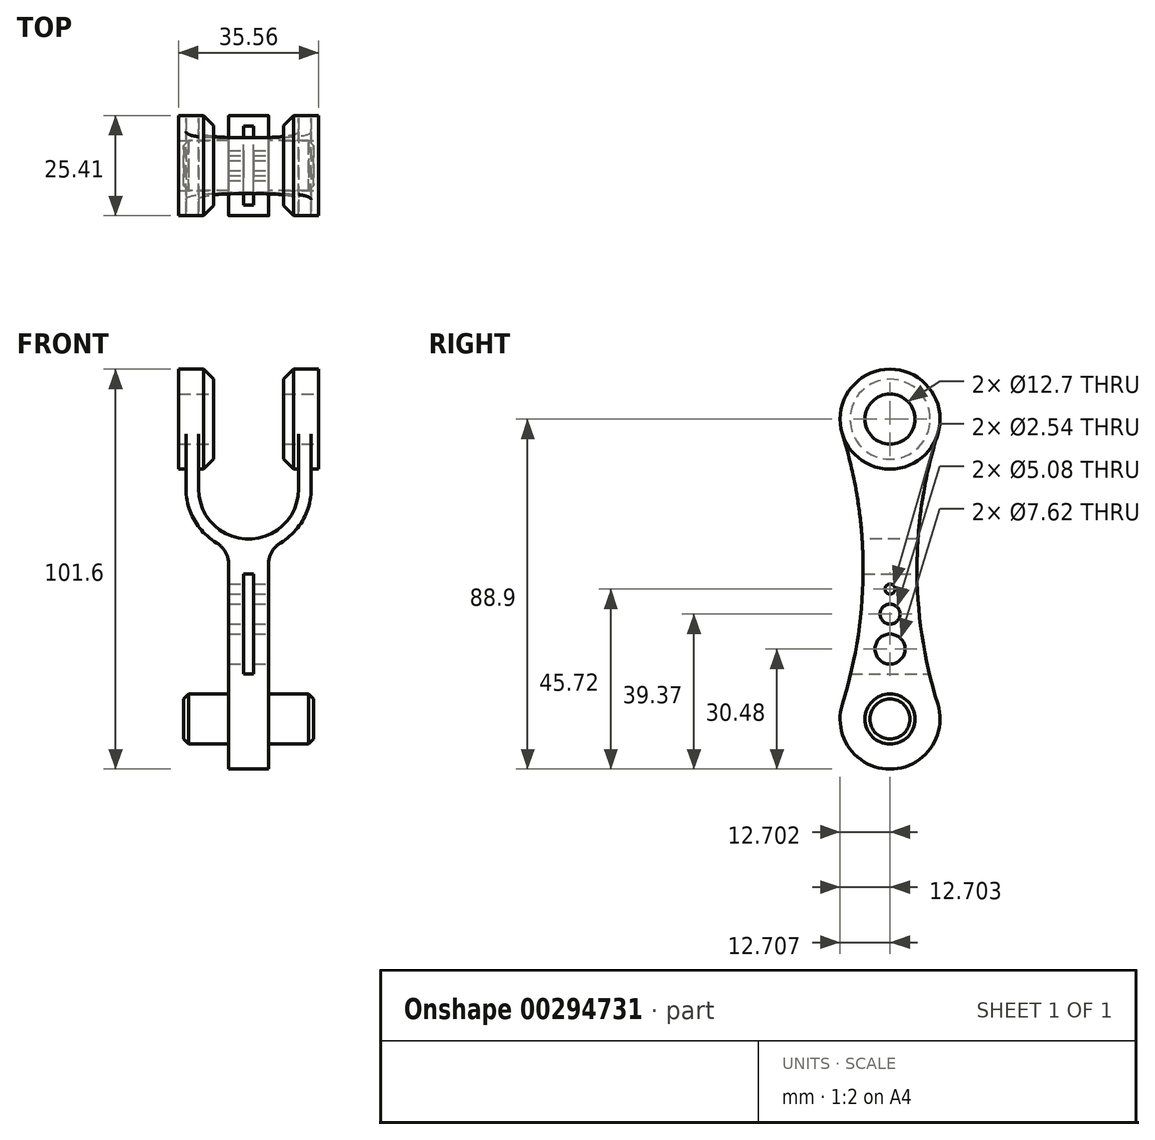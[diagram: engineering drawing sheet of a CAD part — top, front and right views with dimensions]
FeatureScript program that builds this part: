
annotation { "Feature Type Name" : "Feature", "Feature Type Description" : "" }
export const myFeature = defineFeature(function(context is Context, id is Id, definition is map)
    precondition{}
    {
        {
            var Q0;
            Q0=qCreatedBy(makeId("Front.planeOp"),FACE);
            var sketch = newSketch(context, id + "F0", { "sketchPlane" : qUnion([Q0])});
            skPoint(sketch, "E0.middle", {"position": v(0, 0) * mm});
            skArc(sketch, "E1", {"start": v(-8.17, -19.4) * mm, "mid": v(-13.82, -25.2) * mm, "end": v(-15.88, -33.02) * mm});
            skLineSegment(sketch, "E2.bottom", {"start": v(-5.08, 2.35) * mm, "end": v(5.08, 2.35) * mm});
            skLineSegment(sketch, "E2.left", {"start": v(-5.08, 2.35) * mm, "end": v(-5.08, -13.95) * mm});
            skLineSegment(sketch, "E2.right", {"start": v(5.08, 2.35) * mm, "end": v(5.08, -13.95) * mm});
            skArc(sketch, "E3", {"start": v(12.7, -33.02) * mm, "mid": v(0, -20.32) * mm, "end": v(-12.7, -33.02) * mm});
            skLineSegment(sketch, "E4.top", {"start": v(14.22, -50.8) * mm, "end": v(14.36, -50.8) * mm});
            skLineSegment(sketch, "E4.left", {"start": v(12.7, -33.02) * mm, "end": v(12.7, -49.28) * mm});
            skLineSegment(sketch, "E4.right", {"start": v(15.88, -33.02) * mm, "end": v(15.88, -49.28) * mm});
            skLineSegment(sketch, "E5.top", {"start": v(-14.36, -50.8) * mm, "end": v(-14.22, -50.8) * mm});
            skLineSegment(sketch, "E5.left", {"start": v(-15.88, -33.02) * mm, "end": v(-15.88, -49.28) * mm});
            skLineSegment(sketch, "E5.right", {"start": v(-12.7, -33.02) * mm, "end": v(-12.7, -49.28) * mm});
            skArc(sketch, "E6.trimOffspring", {"start": v(15.88, -33.02) * mm, "mid": v(13.82, -25.2) * mm, "end": v(8.17, -19.4) * mm});
            skPoint(sketch, "E7.visualSharp", {"position": v(-5.08, -17.97) * mm});
            skArc(sketch, "E7.filletArc", {"start": v(-8.17, -19.4) * mm, "mid": v(-5.9, -17.08) * mm, "end": v(-5.08, -13.95) * mm});
            skPoint(sketch, "E8.visualSharp", {"position": v(5.08, -17.97) * mm});
            skArc(sketch, "E8.filletArc", {"start": v(5.08, -13.95) * mm, "mid": v(5.9, -17.08) * mm, "end": v(8.17, -19.4) * mm});
            skArc(sketch, "E9.filletArc", {"start": v(12.7, -49.28) * mm, "mid": v(13.15, -50.35) * mm, "end": v(14.22, -50.8) * mm});
            skArc(sketch, "E10.filletArc", {"start": v(14.36, -50.8) * mm, "mid": v(15.44, -50.35) * mm, "end": v(15.88, -49.28) * mm});
            skArc(sketch, "E11.filletArc", {"start": v(-15.88, -49.28) * mm, "mid": v(-15.44, -50.35) * mm, "end": v(-14.36, -50.8) * mm});
            skArc(sketch, "E12.filletArc", {"start": v(-14.22, -50.8) * mm, "mid": v(-13.15, -50.35) * mm, "end": v(-12.7, -49.28) * mm});
            skSolve(sketch);
        }
        {
            var Q0;
            Q0=qSketchRegion(id+"F0",true);
            extrude(context, id + "F1", {"entities" : qUnion([Q0]), "endBound" : BoundingType.SYMMETRIC, "depth" : 38.1 * mm});
        }
        {
            var Q0;
            Q0=qCreatedBy(makeId("Right.planeOp"),FACE);
            var sketch = newSketch(context, id + "F2", { "sketchPlane" : qUnion([Q0])});
            skCircle(sketch, "E13", {"center": v(0, -50.8) * mm, "radius": 6.35 * mm});
            skSolve(sketch);
        }
        {
            var Q0;
            Q0=qCreatedBy(makeId("Right.planeOp"),FACE);
            var sketch = newSketch(context, id + "F3", { "sketchPlane" : qUnion([Q0])});
            skCircle(sketch, "E14", {"center": v(0, -50.8) * mm, "radius": 12.7 * mm});
            skSolve(sketch);
        }
        {
            var Q0;
            Q0=qSketchRegion(id+"F3",true);
            extrude(context, id + "F4", {"entities" : qUnion([Q0]), "operationType" : NewBodyOperationType.ADD, "endBound" : BoundingType.SYMMETRIC, "depth" : 35.56 * mm});
        }
        {
            var Q0;
            Q0=qCreatedBy(makeId("Front.planeOp"),FACE);
            var sketch = newSketch(context, id + "F5", { "sketchPlane" : qUnion([Q0])});
            skLineSegment(sketch, "E15.bottom", {"start": v(8.9, -69.85) * mm, "end": v(-8.89, -69.85) * mm});
            skLineSegment(sketch, "E15.top", {"start": v(8.9, -31.75) * mm, "end": v(-8.89, -31.75) * mm});
            skLineSegment(sketch, "E15.left", {"start": v(8.9, -69.85) * mm, "end": v(8.9, -31.75) * mm});
            skLineSegment(sketch, "E15.right", {"start": v(-8.89, -69.85) * mm, "end": v(-8.89, -31.75) * mm});
            skPoint(sketch, "E15.middle", {"position": v(0, -50.8) * mm});
            skSolve(sketch);
        }
        {
            var Q0;
            Q0=qSketchRegion(id+"F2",true);
            extrude(context, id + "F6", {"entities" : qUnion([Q0]), "operationType" : NewBodyOperationType.REMOVE, "endBound" : BoundingType.SYMMETRIC, "oppositeDirection" : true, "depth" : 76.2 * mm});
        }
        {
            var Q0;
            Q0=qSketchRegion(id+"F5",true);
            extrude(context, id + "F7", {"entities" : qUnion([Q0]), "operationType" : NewBodyOperationType.REMOVE, "endBound" : BoundingType.SYMMETRIC, "oppositeDirection" : true, "depth" : 38.1 * mm});
        }
        {
            var Q0;
            Q0=makeQuery(id+"F7.boolean.opBoolean","INTERSECT",EDGE,{"derivedFrom":[makeQuery(id+"F4.opExtrude","SWEPT_FACE",FACE,{"disambiguationData":[OSD([sQuery(id+"F3.wireOp",EDGE,"E14")])]}),makeQuery(id+"F7.opExtrude","SWEPT_FACE",FACE,{"disambiguationData":[OSD([sQuery(id+"F5.wireOp",EDGE,"E15.right")])]})]});
            var Q1;
            Q1=makeQuery(id+"F7.boolean.opBoolean","INTERSECT",EDGE,{"derivedFrom":[makeQuery(id+"F4.opExtrude","SWEPT_FACE",FACE,{"disambiguationData":[OSD([sQuery(id+"F3.wireOp",EDGE,"E14")])]}),makeQuery(id+"F7.opExtrude","SWEPT_FACE",FACE,{"disambiguationData":[OSD([sQuery(id+"F5.wireOp",EDGE,"E15.left")])]})]});
            chamfer(context, id + "F8", {"entities" : qUnion([Q0, Q1]), "width" : 2.54 * mm, "tangentPropagation" : true});
        }
        {
            var Q0;
            Q0=qCreatedBy(makeId("Right.planeOp"),FACE);
            var sketch = newSketch(context, id + "F9", { "sketchPlane" : qUnion([Q0])});
            skArc(sketch, "E16", {"start": v(19.05, 25.39) * mm, "mid": v(0, 44.45) * mm, "end": v(-19.05, 25.39) * mm});
            skLineSegment(sketch, "E17.top", {"start": v(-19.05, -0.01) * mm, "end": v(19.05, -0.01) * mm});
            skLineSegment(sketch, "E17.left", {"start": v(-19.05, 25.39) * mm, "end": v(-19.05, -0.01) * mm});
            skLineSegment(sketch, "E17.right", {"start": v(19.05, 25.39) * mm, "end": v(19.05, -0.01) * mm});
            skSolve(sketch);
        }
        {
            var Q0;
            Q0=qSketchRegion(id+"F9",true);
            extrude(context, id + "F10", {"entities" : qUnion([Q0]), "operationType" : NewBodyOperationType.ADD, "endBound" : BoundingType.SYMMETRIC, "depth" : 10.16 * mm});
        }
        {
            var Q0;
            Q0=qCreatedBy(makeId("Right.planeOp"),FACE);
            var sketch = newSketch(context, id + "F11", { "sketchPlane" : qUnion([Q0])});
            skCircle(sketch, "E18", {"center": v(0, 25.4) * mm, "radius": 6.35 * mm});
            skSolve(sketch);
        }
        {
            var Q0;
            Q0=qSketchRegion(id+"F11",true);
            extrude(context, id + "F12", {"entities" : qUnion([Q0]), "operationType" : NewBodyOperationType.ADD, "endBound" : BoundingType.SYMMETRIC, "depth" : 33.02 * mm});
        }
        {
            var Q0;
            Q0=makeQuery(id+"F12.opExtrude","CAP_EDGE",EDGE,{"disambiguationData":[OSD([sQuery(id+"F11.wireOp",EDGE,"E18")])],"isStart":true});
            var Q1;
            Q1=makeQuery(id+"F12.opExtrude","CAP_EDGE",EDGE,{"disambiguationData":[OSD([sQuery(id+"F11.wireOp",EDGE,"E18")])],"isStart":false});
            chamfer(context, id + "F13", {"entities" : qUnion([Q0, Q1]), "width" : 1.27 * mm, "tangentPropagation" : true});
        }
        {
            var Q0;
            Q0=qCreatedBy(makeId("Right.planeOp"),FACE);
            var sketch = newSketch(context, id + "F14", { "sketchPlane" : qUnion([Q0])});
            skArc(sketch, "E19", {"start": v(12.12, 21.6) * mm, "mid": v(0, 38.1) * mm, "end": v(-12.12, 21.6) * mm});
            skArc(sketch, "E20", {"start": v(-12.12, -47) * mm, "mid": v(0, -63.5) * mm, "end": v(12.12, -47) * mm});
            skArc(sketch, "E21", {"start": v(12.12, 21.6) * mm, "mid": v(6.85, -12.7) * mm, "end": v(12.12, -47) * mm});
            skPoint(sketch, "E22.center.orphan", {"position": v(45.72, -6.35) * mm});
            skPoint(sketch, "E23.center.orphan", {"position": v(-45.72, -6.35) * mm});
            skArc(sketch, "E24", {"start": v(-12.12, -47) * mm, "mid": v(-6.85, -12.7) * mm, "end": v(-12.12, 21.6) * mm});
            skSolve(sketch);
        }
        {
            var Q0;
            Q0=qSketchRegion(id+"F14",true);
            extrude(context, id + "F15", {"entities" : qUnion([Q0]), "operationType" : NewBodyOperationType.INTERSECT, "endBound" : BoundingType.SYMMETRIC, "depth" : 76.2 * mm});
        }
        {
            var Q0;
            Q0=qCreatedBy(makeId("Front.planeOp"),FACE);
            var sketch = newSketch(context, id + "F16", { "sketchPlane" : qUnion([Q0])});
            skLineSegment(sketch, "E25.bottom", {"start": v(-1.27, -11.4) * mm, "end": v(1.27, -11.4) * mm});
            skLineSegment(sketch, "E25.top", {"start": v(-1.27, 14) * mm, "end": v(1.27, 14) * mm});
            skLineSegment(sketch, "E25.left", {"start": v(-1.27, -11.4) * mm, "end": v(-1.27, 14) * mm});
            skLineSegment(sketch, "E25.right", {"start": v(1.27, -11.4) * mm, "end": v(1.27, 14) * mm});
            skSolve(sketch);
        }
        {
            var Q0;
            Q0=qSketchRegion(id+"F16",true);
            extrude(context, id + "F17", {"entities" : qUnion([Q0]), "operationType" : NewBodyOperationType.REMOVE, "endBound" : BoundingType.SYMMETRIC, "oppositeDirection" : true, "depth" : 50.8 * mm});
        }
        {
            var Q0;
            Q0=qCreatedBy(makeId("Right.planeOp"),FACE);
            var sketch = newSketch(context, id + "F18", { "sketchPlane" : qUnion([Q0])});
            skCircle(sketch, "E26", {"center": v(0, 7.62) * mm, "radius": 3.81 * mm});
            skCircle(sketch, "E27", {"center": v(0, -1.27) * mm, "radius": 2.54 * mm});
            skCircle(sketch, "E28", {"center": v(0, -7.62) * mm, "radius": 1.27 * mm});
            skSolve(sketch);
        }
        {
            var Q0;
            Q0=qSketchRegion(id+"F18",true);
            extrude(context, id + "F19", {"entities" : qUnion([Q0]), "operationType" : NewBodyOperationType.REMOVE, "endBound" : BoundingType.SYMMETRIC, "oppositeDirection" : true, "depth" : 25.4 * mm});
        }
        {
            var Q0;
            Q0=makeQuery(id+"F1.opExtrude","SWEPT_BODY",BODY,{"disambiguationData":[OSD([sQuery(id+"F0.wireOp",EDGE,"E1"),sQuery(id+"F0.wireOp",EDGE,"E2.bottom"),sQuery(id+"F0.wireOp",EDGE,"E2.left"),sQuery(id+"F0.wireOp",EDGE,"E2.right"),sQuery(id+"F0.wireOp",EDGE,"E3"),sQuery(id+"F0.wireOp",EDGE,"E4.top"),sQuery(id+"F0.wireOp",EDGE,"E4.left"),sQuery(id+"F0.wireOp",EDGE,"E4.right"),sQuery(id+"F0.wireOp",EDGE,"E5.top"),sQuery(id+"F0.wireOp",EDGE,"E5.left"),sQuery(id+"F0.wireOp",EDGE,"E5.right"),sQuery(id+"F0.wireOp",EDGE,"E6.trimOffspring"),sQuery(id+"F0.wireOp",EDGE,"E7.filletArc"),sQuery(id+"F0.wireOp",EDGE,"E8.filletArc"),sQuery(id+"F0.wireOp",EDGE,"E9.filletArc"),sQuery(id+"F0.wireOp",EDGE,"E10.filletArc"),sQuery(id+"F0.wireOp",EDGE,"E11.filletArc"),sQuery(id+"F0.wireOp",EDGE,"E12.filletArc")])]});
            var Q1;
            {var subQ0=sQuery(id+"F11.wireOp",EDGE,"E18");Q1=makeQuery(id+"F13.opChamfer","BLEND_EDGE",EDGE,{"blendedFrom":[makeQuery(id+"F12.opExtrude","CAP_EDGE",EDGE,{"disambiguationData":[OSD([subQ0])],"isStart":false}),makeQuery(id+"F12.boolean.opBoolean","SPLIT",FACE,{"disambiguationData":[TD([makeQuery(id+"F1.opExtrude","SWEPT_FACE",FACE,{"disambiguationData":[OSD([sQuery(id+"F0.wireOp",EDGE,"E2.right")])]})])],"derivedFrom":makeQuery(id+"F12.opExtrude","SWEPT_FACE",FACE,{"disambiguationData":[OSD([subQ0])]})})],"blendedInto":[makeQuery(id+"F12.boolean.opBoolean","SPLIT",FACE,{"disambiguationData":[TD([makeQuery(id+"F1.opExtrude","SWEPT_FACE",FACE,{"disambiguationData":[OSD([sQuery(id+"F0.wireOp",EDGE,"E2.right")])]})])],"derivedFrom":makeQuery(id+"F12.opExtrude","SWEPT_FACE",FACE,{"disambiguationData":[OSD([subQ0])]})})]});}
            transform(context, id + "F20", {"entities" : qUnion([Q0]), "transformType" : TransformType.ROTATION, "transformAxis" : qUnion([Q1]), "angle" : 3.14 * radian, "makeCopy" : false});
        }
        {
            var Q0;
            Q0=qCreatedBy(makeId("Front.planeOp"),FACE);
            var sketch = newSketch(context, id + "F21", { "sketchPlane" : qUnion([Q0])});
            skLineSegment(sketch, "E29", {"start": v(17.78, 101.6) * mm, "end": v(-17.78, 101.6) * mm, "construction": true});
            skLineSegment(sketch, "E30", {"start": v(0, 0) * mm, "end": v(0, 101.6) * mm, "construction": true});
            skSolve(sketch);
        }
        {
            var Q0;
            Q0=makeQuery(id+"F1.opExtrude","SWEPT_BODY",BODY,{"disambiguationData":[OSD([sQuery(id+"F0.wireOp",EDGE,"E1"),sQuery(id+"F0.wireOp",EDGE,"E2.bottom"),sQuery(id+"F0.wireOp",EDGE,"E2.left"),sQuery(id+"F0.wireOp",EDGE,"E2.right"),sQuery(id+"F0.wireOp",EDGE,"E3"),sQuery(id+"F0.wireOp",EDGE,"E4.top"),sQuery(id+"F0.wireOp",EDGE,"E4.left"),sQuery(id+"F0.wireOp",EDGE,"E4.right"),sQuery(id+"F0.wireOp",EDGE,"E5.top"),sQuery(id+"F0.wireOp",EDGE,"E5.left"),sQuery(id+"F0.wireOp",EDGE,"E5.right"),sQuery(id+"F0.wireOp",EDGE,"E6.trimOffspring"),sQuery(id+"F0.wireOp",EDGE,"E7.filletArc"),sQuery(id+"F0.wireOp",EDGE,"E8.filletArc"),sQuery(id+"F0.wireOp",EDGE,"E9.filletArc"),sQuery(id+"F0.wireOp",EDGE,"E10.filletArc"),sQuery(id+"F0.wireOp",EDGE,"E11.filletArc"),sQuery(id+"F0.wireOp",EDGE,"E12.filletArc")])]});
            var Q1;
            Q1=sQuery(id+"F21.wireOp",EDGE,"E30");
            transform(context, id + "F22", {"entities" : qUnion([Q0]), "transformType" : TransformType.TRANSLATION_ENTITY, "oppositeDirectionEntity" : true, "transformLine" : qUnion([Q1]), "makeCopy" : false});
        }
    });
